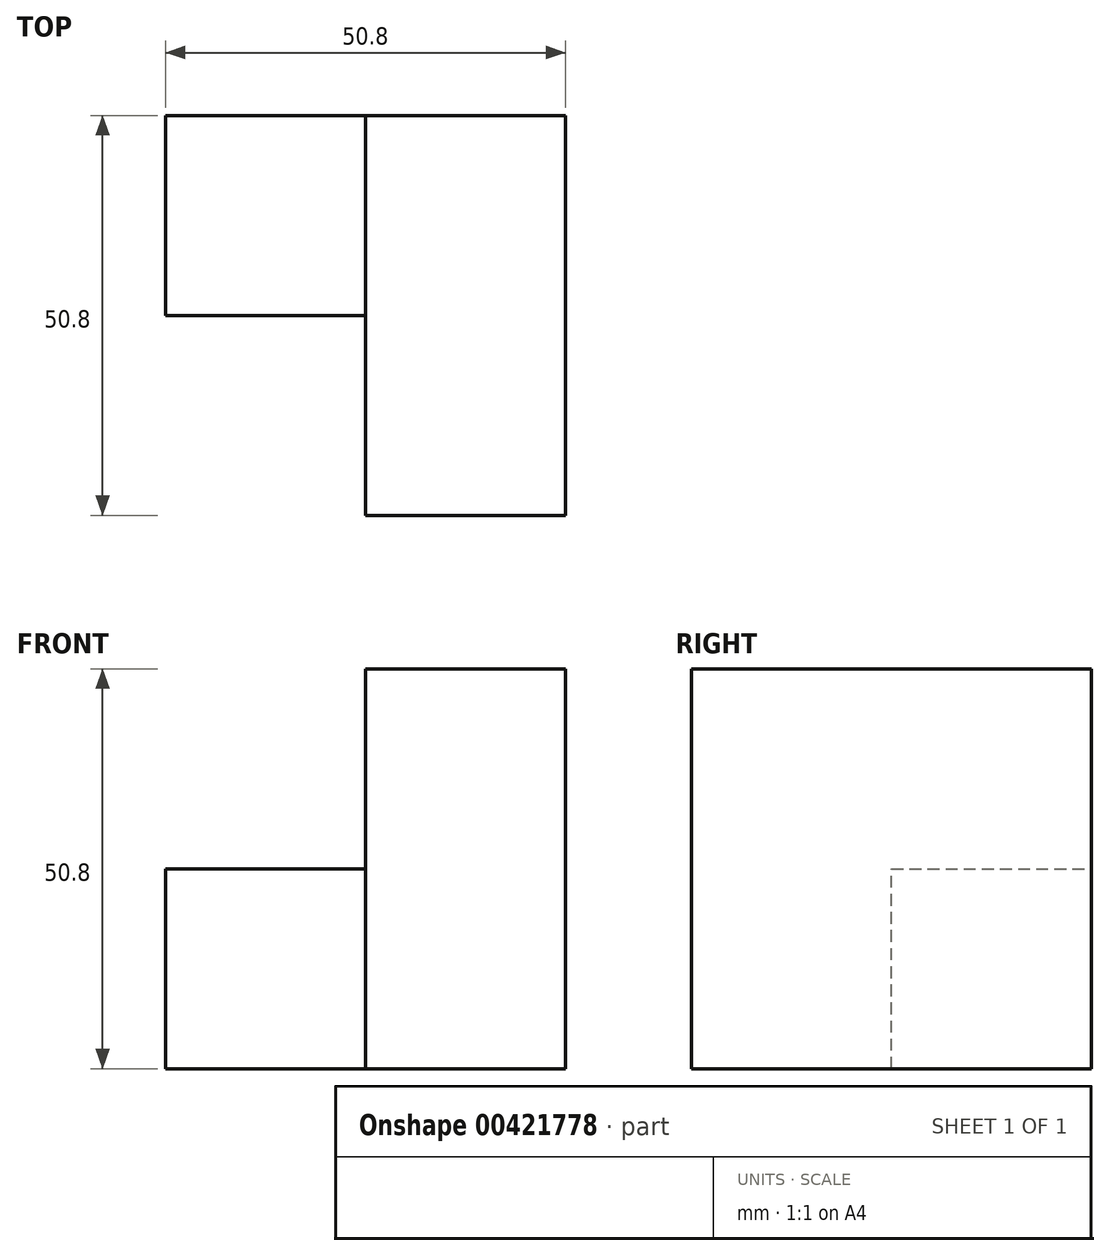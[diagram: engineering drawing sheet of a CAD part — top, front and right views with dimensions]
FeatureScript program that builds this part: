
annotation { "Feature Type Name" : "Feature", "Feature Type Description" : "" }
export const myFeature = defineFeature(function(context is Context, id is Id, definition is map)
    precondition{}
    {
        {
            var Q0;
            Q0=qCreatedBy(makeId("Front.planeOp"),FACE);
            var sketch = newSketch(context, id + "F0", { "sketchPlane" : qUnion([Q0])});
            skLineSegment(sketch, "E0", {"start": v(0, 0) * mm, "end": v(0, 50.8) * mm});
            skLineSegment(sketch, "E1", {"start": v(0, 50.8) * mm, "end": v(-25.4, 50.8) * mm});
            skLineSegment(sketch, "E2", {"start": v(-25.4, 50.8) * mm, "end": v(-25.4, 0) * mm});
            skLineSegment(sketch, "E3", {"start": v(-25.4, 0) * mm, "end": v(0, 0) * mm});
            skSolve(sketch);
        }
        {
            var Q0;
            Q0=makeQuery(id+"F0.imprint","IMPRINT",FACE,{"disambiguationData":[TD([[makeQuery(id+"F0.imprint","IMPRINT",EDGE,{"derivedFrom":sQuery(id+"F0.wireOp",EDGE,"E0")}),1.0]])]});
            extrude(context, id + "F1", {"entities" : qUnion([Q0]), "depth" : 50.8 * mm});
        }
        {
            var Q0;
            Q0=makeQuery(id+"F1.opExtrude","SWEPT_FACE",FACE,{"disambiguationData":[OSD([sQuery(id+"F0.wireOp",EDGE,"E2")])]});
            var sketch = newSketch(context, id + "F2", { "sketchPlane" : qUnion([Q0])});
            skLineSegment(sketch, "E4", {"start": v(0, 0) * mm, "end": v(25.4, 0) * mm});
            skLineSegment(sketch, "E5", {"start": v(25.4, 0) * mm, "end": v(25.4, 25.4) * mm});
            skLineSegment(sketch, "E6", {"start": v(25.4, 25.4) * mm, "end": v(0, 25.4) * mm});
            skPoint(sketch, "E6.endSnap0", {"position": v(0, 25.4) * mm});
            skLineSegment(sketch, "E7", {"start": v(0, 25.4) * mm, "end": v(0, 0) * mm});
            skSolve(sketch);
        }
        {
            var Q0;
            Q0=makeQuery(id+"F2.imprint","IMPRINT",FACE,{"disambiguationData":[TD([[makeQuery(id+"F2.imprint","IMPRINT",EDGE,{"derivedFrom":sQuery(id+"F2.wireOp",EDGE,"E4")}),-1.0]])]});
            extrude(context, id + "F3", {"entities" : qUnion([Q0]), "operationType" : NewBodyOperationType.ADD, "depth" : 25.4 * mm});
        }
    });
